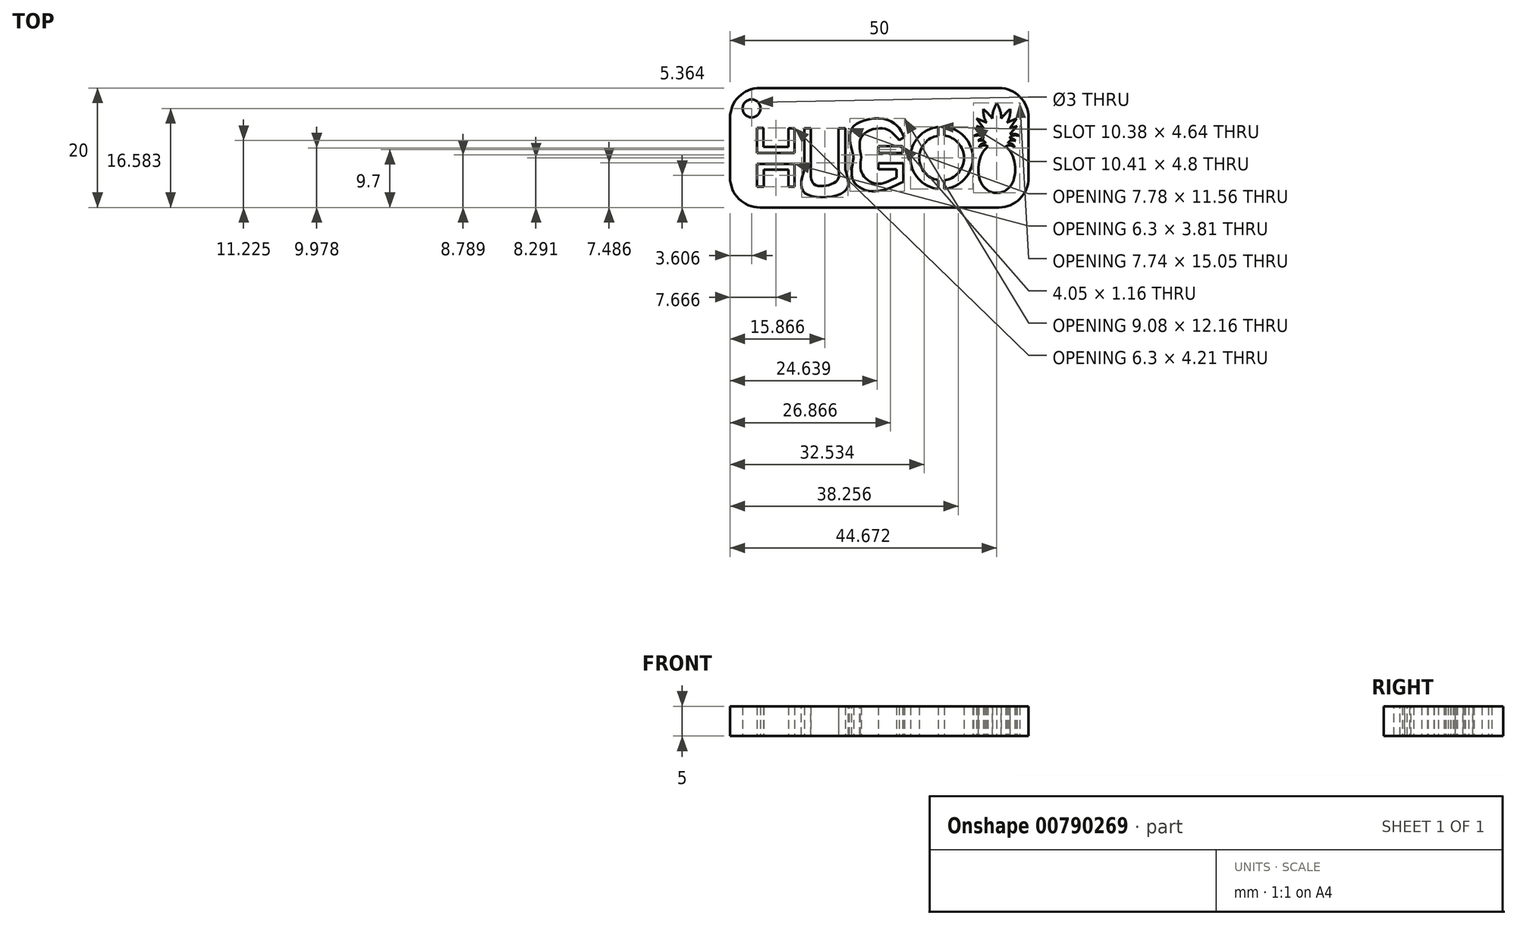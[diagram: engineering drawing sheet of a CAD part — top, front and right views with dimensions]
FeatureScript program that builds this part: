
annotation { "Feature Type Name" : "Feature", "Feature Type Description" : "" }
export const myFeature = defineFeature(function(context is Context, id is Id, definition is map)
    precondition{}
    {
        {
            var Q0;
            Q0=qCreatedBy(makeId("Top.planeOp"),FACE);
            var sketch = newSketch(context, id + "F0", { "sketchPlane" : qUnion([Q0])});
            skLineSegment(sketch, "E0.bottom", {"start": v(-19.84, 5.89) * mm, "end": v(20.16, 5.89) * mm});
            skLineSegment(sketch, "E0.top", {"start": v(-19.84, -14.11) * mm, "end": v(20.16, -14.11) * mm});
            skLineSegment(sketch, "E0.left", {"start": v(-24.84, 0.89) * mm, "end": v(-24.84, -9.11) * mm});
            skLineSegment(sketch, "E0.right", {"start": v(25.16, 0.89) * mm, "end": v(25.16, -9.11) * mm});
            skPoint(sketch, "E1.visualSharp", {"position": v(-24.84, 5.89) * mm});
            skArc(sketch, "E1.filletArc", {"start": v(-19.84, 5.89) * mm, "mid": v(-23.37, 4.42) * mm, "end": v(-24.84, 0.89) * mm});
            skPoint(sketch, "E2.visualSharp", {"position": v(-24.84, -14.11) * mm});
            skArc(sketch, "E2.filletArc", {"start": v(-24.84, -9.11) * mm, "mid": v(-23.37, -12.65) * mm, "end": v(-19.84, -14.11) * mm});
            skPoint(sketch, "E3.visualSharp", {"position": v(25.16, -14.11) * mm});
            skArc(sketch, "E3.filletArc", {"start": v(20.16, -14.11) * mm, "mid": v(23.7, -12.65) * mm, "end": v(25.16, -9.11) * mm});
            skPoint(sketch, "E4.visualSharp", {"position": v(25.16, 5.89) * mm});
            skArc(sketch, "E4.filletArc", {"start": v(25.16, 0.89) * mm, "mid": v(23.7, 4.42) * mm, "end": v(20.16, 5.89) * mm});
            skLineSegment(sketch, "E5", {"start": v(-18.48, 0.56) * mm, "end": v(-18.48, -3.26) * mm});
            skLineSegment(sketch, "E6", {"start": v(-18.48, -3.26) * mm, "end": v(-12.75, -3.26) * mm});
            skLineSegment(sketch, "E7", {"start": v(-12.75, -3.26) * mm, "end": v(-12.75, 0.5) * mm});
            skLineSegment(sketch, "E8", {"start": v(-12.75, 0.5) * mm, "end": v(-13.71, 0.5) * mm});
            skLineSegment(sketch, "E9", {"start": v(-13.71, 0.5) * mm, "end": v(-13.71, -2.33) * mm});
            skLineSegment(sketch, "E10", {"start": v(-13.71, -2.33) * mm, "end": v(-17.48, -2.33) * mm});
            skLineSegment(sketch, "E11", {"start": v(-17.48, -2.33) * mm, "end": v(-17.48, 0.56) * mm});
            skLineSegment(sketch, "E12", {"start": v(-17.48, 0.56) * mm, "end": v(-18.48, 0.56) * mm});
            skLineSegment(sketch, "E13", {"start": v(-18.48, -4.94) * mm, "end": v(-12.75, -4.94) * mm});
            skLineSegment(sketch, "E14", {"start": v(-12.75, -4.94) * mm, "end": v(-12.75, -8.41) * mm});
            skLineSegment(sketch, "E15", {"start": v(-12.75, -8.41) * mm, "end": v(-13.7, -8.41) * mm});
            skLineSegment(sketch, "E16", {"start": v(-13.7, -8.41) * mm, "end": v(-13.7, -5.81) * mm});
            skLineSegment(sketch, "E17", {"start": v(-13.7, -5.81) * mm, "end": v(-17.44, -5.81) * mm});
            skLineSegment(sketch, "E18", {"start": v(-17.44, -5.81) * mm, "end": v(-17.44, -8.41) * mm});
            skLineSegment(sketch, "E19", {"start": v(-10.28, 0.5) * mm, "end": v(-10.28, -5.77) * mm});
            skLineSegment(sketch, "E20", {"start": v(-10.28, 0.5) * mm, "end": v(-11.25, 0.5) * mm});
            skLineSegment(sketch, "E21", {"start": v(-11.25, 0.5) * mm, "end": v(-11.25, -5.77) * mm});
            skFitSpline(sketch, "E22", {"points": [v(-11.25, -5.77) * mm, v(-5.06, -5.77) * mm], "startDerivative": vector(0.22, -10.8) * mm, "endDerivative": vector(0.13, 9.96) * mm});
            skLineSegment(sketch, "E23", {"start": v(-5.06, -5.77) * mm, "end": v(-5.06, 0.5) * mm});
            skLineSegment(sketch, "E24", {"start": v(-5.06, 0.5) * mm, "end": v(-6.09, 0.5) * mm});
            skLineSegment(sketch, "E25", {"start": v(-6.09, 0.5) * mm, "end": v(-6.09, -5.77) * mm});
            skFitSpline(sketch, "E26", {"points": [v(-10.28, -5.77) * mm, v(-6.09, -5.77) * mm], "startDerivative": vector(1.86, -6.96) * mm, "endDerivative": vector(0.87, 5.34) * mm});
            skLineSegment(sketch, "E27", {"start": v(0, -2.21) * mm, "end": v(0, -3.26) * mm});
            skLineSegment(sketch, "E28", {"start": v(0, -3.26) * mm, "end": v(3.68, -3.26) * mm});
            skLineSegment(sketch, "E29", {"start": v(3.68, -3.26) * mm, "end": v(3.68, -2.21) * mm});
            skLineSegment(sketch, "E30", {"start": v(3.68, -2.21) * mm, "end": v(0, -2.21) * mm});
            skLineSegment(sketch, "E31", {"start": v(0, -4.83) * mm, "end": v(3.79, -4.83) * mm});
            skLineSegment(sketch, "E32", {"start": v(3.79, -4.83) * mm, "end": v(3.79, -7.64) * mm});
            skLineSegment(sketch, "E33", {"start": v(0, -4.83) * mm, "end": v(0, -5.76) * mm});
            skLineSegment(sketch, "E34", {"start": v(0, -5.76) * mm, "end": v(2.74, -5.76) * mm});
            skLineSegment(sketch, "E35", {"start": v(2.74, -5.76) * mm, "end": v(2.74, -6.98) * mm});
            skLineSegment(sketch, "E36", {"start": v(3.16, -1.32) * mm, "end": v(3.95, -0.82) * mm});
            skCircle(sketch, "E37", {"center": v(9.63, -4.02) * mm, "radius": 4.75 * mm});
            skCircle(sketch, "E38", {"center": v(9.63, -4.02) * mm, "radius": 3.42 * mm});
            skFitSpline(sketch, "E39", {"points": [v(18.36, -3.9) * mm, v(19.83, -11.66) * mm], "startDerivative": vector(-7.27, -5.5) * mm, "endDerivative": vector(11.16, -0.02) * mm});
            skFitSpline(sketch, "E40", {"points": [v(18.36, -3.9) * mm, v(16.84, -4.02) * mm], "startDerivative": vector(-0.8, 0.54) * mm, "endDerivative": vector(-2.6, -1.65) * mm});
            skFitSpline(sketch, "E41", {"points": [v(16.84, -4.02) * mm, v(17.98, -3.35) * mm], "startDerivative": vector(0.44, 1.12) * mm, "endDerivative": vector(2.28, -0.1) * mm});
            skFitSpline(sketch, "E42", {"points": [v(17.98, -3.35) * mm, v(16.69, -2.95) * mm], "startDerivative": vector(-0.63, 1.38) * mm, "endDerivative": vector(-2.13, -0.57) * mm});
            skFitSpline(sketch, "E43", {"points": [v(16.69, -2.95) * mm, v(17.7, -2.5) * mm], "startDerivative": vector(0.87, 1.1) * mm, "endDerivative": vector(1.28, 0.15) * mm});
            skFitSpline(sketch, "E44", {"points": [v(17.7, -2.5) * mm, v(15.96, -2.15) * mm], "startDerivative": vector(-1.13, 1.33) * mm, "endDerivative": vector(-2.84, -0.77) * mm});
            skFitSpline(sketch, "E45", {"points": [v(15.96, -2.15) * mm, v(17.66, -1.83) * mm], "startDerivative": vector(1.53, 0.99) * mm, "endDerivative": vector(2.26, -0.37) * mm});
            skLineSegment(sketch, "E46", {"start": v(17.66, -1.83) * mm, "end": v(16.45, -0.46) * mm});
            skLineSegment(sketch, "E47", {"start": v(16.45, -0.46) * mm, "end": v(17.66, -0.87) * mm});
            skLineSegment(sketch, "E48", {"start": v(17.66, -0.87) * mm, "end": v(16.47, 0.8) * mm});
            skLineSegment(sketch, "E49", {"start": v(16.47, 0.8) * mm, "end": v(18.15, 0.08) * mm});
            skFitSpline(sketch, "E50", {"points": [v(18.15, 0.08) * mm, v(17.55, 2.36) * mm], "startDerivative": vector(-1.53, 2.07) * mm, "endDerivative": vector(-0.1, 2.34) * mm});
            skFitSpline(sketch, "E51", {"points": [v(17.55, 2.36) * mm, v(19.09, 0.8) * mm], "startDerivative": vector(1.69, -1.38) * mm, "endDerivative": vector(1.38, -1.77) * mm});
            skFitSpline(sketch, "E52", {"points": [v(19.09, 0.8) * mm, v(19.83, 3.4) * mm], "startDerivative": vector(-0.13, 3.12) * mm, "endDerivative": vector(1.04, 1.95) * mm});
            skLineSegment(sketch, "E53", {"start": v(19.83, 3.4) * mm, "end": v(19.83, -11.62) * mm});
            skFitSpline(sketch, "E54.MirrorCS", {"points": [v(21.95, -2.5) * mm, v(23.7, -2.15) * mm], "startDerivative": vector(1.13, 1.33) * mm, "endDerivative": vector(2.84, -0.77) * mm});
            skFitSpline(sketch, "E55.MirrorCS", {"points": [v(23.7, -2.15) * mm, v(22, -1.83) * mm], "startDerivative": vector(-1.53, 0.99) * mm, "endDerivative": vector(-2.26, -0.37) * mm});
            skFitSpline(sketch, "E56.MirrorCS", {"points": [v(20.58, 0.8) * mm, v(19.83, 3.4) * mm], "startDerivative": vector(0.13, 3.12) * mm, "endDerivative": vector(-1.04, 1.95) * mm});
            skFitSpline(sketch, "E57.MirrorCS", {"points": [v(22.97, -2.95) * mm, v(21.95, -2.5) * mm], "startDerivative": vector(-0.87, 1.1) * mm, "endDerivative": vector(-1.28, 0.15) * mm});
            skFitSpline(sketch, "E58.MirrorCS", {"points": [v(21.3, -3.9) * mm, v(22.83, -4.02) * mm], "startDerivative": vector(0.8, 0.54) * mm, "endDerivative": vector(2.6, -1.65) * mm});
            skFitSpline(sketch, "E59.MirrorCS", {"points": [v(22.11, 2.36) * mm, v(20.58, 0.8) * mm], "startDerivative": vector(-1.69, -1.38) * mm, "endDerivative": vector(-1.38, -1.77) * mm});
            skFitSpline(sketch, "E60.MirrorCS", {"points": [v(22.83, -4.02) * mm, v(21.68, -3.35) * mm], "startDerivative": vector(-0.44, 1.12) * mm, "endDerivative": vector(-2.28, -0.1) * mm});
            skLineSegment(sketch, "E61.MirrorCS", {"start": v(22, -1.83) * mm, "end": v(23.22, -0.46) * mm});
            skFitSpline(sketch, "E62.MirrorCS", {"points": [v(21.51, 0.08) * mm, v(22.11, 2.36) * mm], "startDerivative": vector(1.53, 2.07) * mm, "endDerivative": vector(0.1, 2.34) * mm});
            skFitSpline(sketch, "E63.MirrorCS", {"points": [v(21.68, -3.35) * mm, v(22.97, -2.95) * mm], "startDerivative": vector(0.63, 1.38) * mm, "endDerivative": vector(2.13, -0.57) * mm});
            skLineSegment(sketch, "E64.MirrorCS", {"start": v(23.2, 0.8) * mm, "end": v(21.51, 0.08) * mm});
            skLineSegment(sketch, "E65.MirrorCS", {"start": v(59.5, 5.89) * mm, "end": v(19.5, 5.89) * mm});
            skLineSegment(sketch, "E66.MirrorCS", {"start": v(22, -0.87) * mm, "end": v(23.2, 0.8) * mm});
            skFitSpline(sketch, "E67.MirrorCS", {"points": [v(21.3, -3.9) * mm, v(19.83, -11.66) * mm], "startDerivative": vector(7.27, -5.5) * mm, "endDerivative": vector(-11.16, -0.02) * mm});
            skLineSegment(sketch, "E68.MirrorCS", {"start": v(23.22, -0.46) * mm, "end": v(22, -0.87) * mm});
            skLineSegment(sketch, "E69", {"start": v(-17.44, -8.41) * mm, "end": v(-18.48, -8.41) * mm});
            skLineSegment(sketch, "E70", {"start": v(-18.48, -8.41) * mm, "end": v(-18.48, -4.94) * mm});
            skFitSpline(sketch, "E71", {"points": [v(3.79, -7.64) * mm, v(-3.76, -3.9) * mm], "startDerivative": vector(-13.3, -4.36) * mm, "endDerivative": vector(-0.15, 11.36) * mm});
            skFitSpline(sketch, "E72", {"points": [v(-3.76, -3.9) * mm, v(3.95, -0.82) * mm], "startDerivative": vector(-0.24, 13.91) * mm, "endDerivative": vector(7.19, -7.64) * mm});
            skFitSpline(sketch, "E73", {"points": [v(-2.6, -3.96) * mm, v(2.74, -6.98) * mm], "startDerivative": vector(0.11, -6.75) * mm, "endDerivative": vector(9.48, 2.83) * mm});
            skFitSpline(sketch, "E74", {"points": [v(-2.6, -3.96) * mm, v(3.16, -1.32) * mm], "startDerivative": vector(0.46, 10.07) * mm, "endDerivative": vector(6.53, -5.23) * mm});
            skLineSegment(sketch, "E75", {"start": v(19.83, -11.62) * mm, "end": v(19.83, -14.11) * mm});
            skLineSegment(sketch, "E76", {"start": v(19.83, 3.4) * mm, "end": v(19.83, 5.89) * mm});
            skLineSegment(sketch, "E77", {"start": v(9.38, -7.43) * mm, "end": v(9.38, -8.76) * mm});
            skLineSegment(sketch, "E78", {"start": v(9.88, -7.43) * mm, "end": v(9.88, -8.76) * mm});
            skLineSegment(sketch, "E79", {"start": v(9.63, -4.02) * mm, "end": v(13.05, -4.02) * mm});
            skLineSegment(sketch, "E80.MirrorCS", {"start": v(9.88, -0.6) * mm, "end": v(9.88, 0.72) * mm});
            skLineSegment(sketch, "E81.MirrorCS", {"start": v(9.38, -0.6) * mm, "end": v(9.38, 0.72) * mm});
            skCircle(sketch, "E82", {"center": v(-21.23, 2.47) * mm, "radius": 1.5 * mm});
            skSolve(sketch);
        }
        {
            var Q0;
            Q0 = qSketchRegion(id + "F0", true);
            var Q1;
            {var subQ0=sQuery(id+"F0.wireOp",EDGE,"E77");Q1=makeQuery(id+"F0.imprint","IMPRINT",FACE,{"disambiguationData":[TD([[makeQuery(id+"F0.imprint","IMPRINT",EDGE,{"derivedFrom":subQ0}),1.0]])]});}
            var Q2;
            {var subQ0=sQuery(id+"F0.wireOp",EDGE,"E38");var subQ5=makeQuery(id+"F0.imprint","IMPRINT",VERTEX,{"derivedFrom":subQ0});Q2=makeQuery(id+"F0.imprint","IMPRINT",FACE,{"disambiguationData":[TD([[makeQuery(id+"F0.imprint","IMPRINT",EDGE,{"disambiguationData":[TD([[subQ5,-1.0]])],"derivedFrom":subQ0}),1.0]])]});}
            var Q3;
            {var subQ0=sQuery(id+"F0.wireOp",EDGE,"E80.MirrorCS");Q3=makeQuery(id+"F0.imprint","IMPRINT",FACE,{"disambiguationData":[TD([[makeQuery(id+"F0.imprint","IMPRINT",EDGE,{"derivedFrom":subQ0}),1.0]])]});}
            var Q4;
            Q4=makeQuery(id+"F0.imprint","IMPRINT",FACE,{"disambiguationData":[TD([[makeQuery(id+"F0.imprint","IMPRINT",EDGE,{"derivedFrom":sQuery(id+"F0.wireOp",EDGE,"E5")}),1.0]])]});
            var Q5;
            Q5=makeQuery(id+"F0.imprint","IMPRINT",FACE,{"disambiguationData":[TD([[makeQuery(id+"F0.imprint","IMPRINT",EDGE,{"derivedFrom":sQuery(id+"F0.wireOp",EDGE,"E13")}),-1.0]])]});
            var Q6;
            Q6=makeQuery(id+"F0.imprint","IMPRINT",FACE,{"disambiguationData":[TD([[makeQuery(id+"F0.imprint","IMPRINT",EDGE,{"derivedFrom":sQuery(id+"F0.wireOp",EDGE,"E19")}),-1.0]])]});
            var Q7;
            Q7=makeQuery(id+"F0.imprint","IMPRINT",FACE,{"disambiguationData":[TD([[makeQuery(id+"F0.imprint","IMPRINT",EDGE,{"derivedFrom":sQuery(id+"F0.wireOp",EDGE,"E31")}),-1.0]])]});
            var Q8;
            Q8=makeQuery(id+"F0.imprint","IMPRINT",FACE,{"disambiguationData":[TD([[makeQuery(id+"F0.imprint","IMPRINT",EDGE,{"derivedFrom":sQuery(id+"F0.wireOp",EDGE,"E27")}),1.0]])]});
            var Q9;
            {var subQ0=sQuery(id+"F0.wireOp",EDGE,"E77");Q9=makeQuery(id+"F0.imprint","IMPRINT",FACE,{"disambiguationData":[TD([[makeQuery(id+"F0.imprint","IMPRINT",EDGE,{"derivedFrom":subQ0}),-1.0]])]});}
            var Q10;
            {var subQ0=sQuery(id+"F0.wireOp",EDGE,"E78");Q10=makeQuery(id+"F0.imprint","IMPRINT",FACE,{"disambiguationData":[TD([[makeQuery(id+"F0.imprint","IMPRINT",EDGE,{"derivedFrom":subQ0}),1.0]])]});}
            extrude(context, id + "F1", {"entities" : qUnion([Q0, Q1, Q2, Q3, Q4, Q5, Q6, Q7, Q8, Q9, Q10]), "depth" : 5 * mm, "offsetDistance" : 25 * mm});
        }
        {
            var Q0;
            Q0=makeQuery(id+"F1.opExtrude","CAP_FACE",FACE,{"disambiguationData":[OSD([sQuery(id+"F0.wireOp",EDGE,"E0.bottom"),sQuery(id+"F0.wireOp",EDGE,"E0.top"),sQuery(id+"F0.wireOp",EDGE,"E0.left"),sQuery(id+"F0.wireOp",EDGE,"E0.right"),sQuery(id+"F0.wireOp",EDGE,"E1.filletArc"),sQuery(id+"F0.wireOp",EDGE,"E2.filletArc"),sQuery(id+"F0.wireOp",EDGE,"E3.filletArc"),sQuery(id+"F0.wireOp",EDGE,"E4.filletArc"),sQuery(id+"F0.wireOp",EDGE,"E5"),sQuery(id+"F0.wireOp",EDGE,"E6"),sQuery(id+"F0.wireOp",EDGE,"E7"),sQuery(id+"F0.wireOp",EDGE,"E8"),sQuery(id+"F0.wireOp",EDGE,"E9"),sQuery(id+"F0.wireOp",EDGE,"E10"),sQuery(id+"F0.wireOp",EDGE,"E11"),sQuery(id+"F0.wireOp",EDGE,"E12"),sQuery(id+"F0.wireOp",EDGE,"E13"),sQuery(id+"F0.wireOp",EDGE,"E14"),sQuery(id+"F0.wireOp",EDGE,"E15"),sQuery(id+"F0.wireOp",EDGE,"E16"),sQuery(id+"F0.wireOp",EDGE,"E17"),sQuery(id+"F0.wireOp",EDGE,"E18"),sQuery(id+"F0.wireOp",EDGE,"E19"),sQuery(id+"F0.wireOp",EDGE,"E20"),sQuery(id+"F0.wireOp",EDGE,"E21"),sQuery(id+"F0.wireOp",EDGE,"E22"),sQuery(id+"F0.wireOp",EDGE,"E23"),sQuery(id+"F0.wireOp",EDGE,"E24"),sQuery(id+"F0.wireOp",EDGE,"E25"),sQuery(id+"F0.wireOp",EDGE,"E26"),sQuery(id+"F0.wireOp",EDGE,"E27"),sQuery(id+"F0.wireOp",EDGE,"E28"),sQuery(id+"F0.wireOp",EDGE,"E29"),sQuery(id+"F0.wireOp",EDGE,"E30"),sQuery(id+"F0.wireOp",EDGE,"E31"),sQuery(id+"F0.wireOp",EDGE,"E32"),sQuery(id+"F0.wireOp",EDGE,"E33"),sQuery(id+"F0.wireOp",EDGE,"E34"),sQuery(id+"F0.wireOp",EDGE,"E35"),sQuery(id+"F0.wireOp",EDGE,"E36"),sQuery(id+"F0.wireOp",EDGE,"E37"),sQuery(id+"F0.wireOp",EDGE,"E38"),sQuery(id+"F0.wireOp",EDGE,"E39"),sQuery(id+"F0.wireOp",EDGE,"E40"),sQuery(id+"F0.wireOp",EDGE,"E41"),sQuery(id+"F0.wireOp",EDGE,"E42"),sQuery(id+"F0.wireOp",EDGE,"E43"),sQuery(id+"F0.wireOp",EDGE,"E44"),sQuery(id+"F0.wireOp",EDGE,"E45"),sQuery(id+"F0.wireOp",EDGE,"E46"),sQuery(id+"F0.wireOp",EDGE,"E47"),sQuery(id+"F0.wireOp",EDGE,"E48"),sQuery(id+"F0.wireOp",EDGE,"E49"),sQuery(id+"F0.wireOp",EDGE,"E50"),sQuery(id+"F0.wireOp",EDGE,"E51"),sQuery(id+"F0.wireOp",EDGE,"E52"),sQuery(id+"F0.wireOp",EDGE,"E54.MirrorCS"),sQuery(id+"F0.wireOp",EDGE,"E55.MirrorCS"),sQuery(id+"F0.wireOp",EDGE,"E56.MirrorCS"),sQuery(id+"F0.wireOp",EDGE,"E57.MirrorCS"),sQuery(id+"F0.wireOp",EDGE,"E58.MirrorCS"),sQuery(id+"F0.wireOp",EDGE,"E59.MirrorCS"),sQuery(id+"F0.wireOp",EDGE,"E60.MirrorCS"),sQuery(id+"F0.wireOp",EDGE,"E61.MirrorCS"),sQuery(id+"F0.wireOp",EDGE,"E62.MirrorCS"),sQuery(id+"F0.wireOp",EDGE,"E63.MirrorCS"),sQuery(id+"F0.wireOp",EDGE,"E64.MirrorCS"),sQuery(id+"F0.wireOp",EDGE,"E65.MirrorCS"),sQuery(id+"F0.wireOp",EDGE,"E66.MirrorCS"),sQuery(id+"F0.wireOp",EDGE,"E67.MirrorCS"),sQuery(id+"F0.wireOp",EDGE,"E68.MirrorCS"),sQuery(id+"F0.wireOp",EDGE,"E69"),sQuery(id+"F0.wireOp",EDGE,"E70"),sQuery(id+"F0.wireOp",EDGE,"E71"),sQuery(id+"F0.wireOp",EDGE,"E72"),sQuery(id+"F0.wireOp",EDGE,"E73"),sQuery(id+"F0.wireOp",EDGE,"E74"),sQuery(id+"F0.wireOp",EDGE,"E77"),sQuery(id+"F0.wireOp",EDGE,"E78"),sQuery(id+"F0.wireOp",EDGE,"E80.MirrorCS"),sQuery(id+"F0.wireOp",EDGE,"E81.MirrorCS"),sQuery(id+"F0.wireOp",EDGE,"E82")])],"isStart":false});
            var sketch = newSketch(context, id + "F2", { "sketchPlane" : qUnion([Q0])});
            skLineSegment(sketch, "E83.0", {"start": v(-13.7, -8.41) * mm, "end": v(-13.7, -5.81) * mm});
            skLineSegment(sketch, "E83.1", {"start": v(3.79, -4.83) * mm, "end": v(3.79, -7.64) * mm});
            skLineSegment(sketch, "E83.2", {"start": v(-13.7, -5.81) * mm, "end": v(-17.44, -5.81) * mm});
            skLineSegment(sketch, "E83.3", {"start": v(-17.44, -5.81) * mm, "end": v(-17.44, -8.41) * mm});
            skLineSegment(sketch, "E83.4", {"start": v(0, -5.76) * mm, "end": v(2.74, -5.76) * mm});
            skLineSegment(sketch, "E83.5", {"start": v(-10.28, 0.5) * mm, "end": v(-10.28, -5.77) * mm});
            skCircle(sketch, "E83.6", {"center": v(9.63, -4.02) * mm, "radius": 4.75 * mm});
            skLineSegment(sketch, "E83.7", {"start": v(-11.25, 0.5) * mm, "end": v(-11.25, -5.77) * mm});
            skCircle(sketch, "E83.8", {"center": v(9.63, -4.02) * mm, "radius": 3.42 * mm});
            skFitSpline(sketch, "E83.9", {"points": [v(-11.25, -5.77) * mm, v(-11.17, -9.38) * mm, v(-5.1, -9.1) * mm, v(-5.06, -5.77) * mm]});
            skLineSegment(sketch, "E83.10", {"start": v(-18.48, -8.41) * mm, "end": v(-18.48, -4.94) * mm});
            skLineSegment(sketch, "E83.11", {"start": v(-5.06, -5.77) * mm, "end": v(-5.06, 0.5) * mm});
            skFitSpline(sketch, "E83.12", {"points": [v(3.79, -7.64) * mm, v(-0.64, -9.1) * mm, v(-3.71, -7.68) * mm, v(-3.76, -3.9) * mm]});
            skFitSpline(sketch, "E83.13", {"points": [v(-3.76, -3.9) * mm, v(-3.84, 0.74) * mm, v(1.55, 1.73) * mm, v(3.95, -0.82) * mm]});
            skFitSpline(sketch, "E83.14", {"points": [v(-2.6, -3.96) * mm, v(-2.45, -0.6) * mm, v(0.99, 0.42) * mm, v(3.16, -1.32) * mm]});
            skFitSpline(sketch, "E83.15", {"points": [v(-10.28, -5.77) * mm, v(-9.66, -8.1) * mm, v(-6.38, -7.55) * mm, v(-6.09, -5.77) * mm]});
            skLineSegment(sketch, "E83.16", {"start": v(-6.09, 0.5) * mm, "end": v(-6.09, -5.77) * mm});
            skFitSpline(sketch, "E83.17", {"points": [v(-2.6, -3.96) * mm, v(-2.56, -6.21) * mm, v(-0.42, -7.93) * mm, v(2.74, -6.98) * mm]});
            skLineSegment(sketch, "E83.18", {"start": v(0, -3.26) * mm, "end": v(3.68, -3.26) * mm});
            skLineSegment(sketch, "E83.19", {"start": v(-13.71, -2.33) * mm, "end": v(-17.48, -2.33) * mm});
            skLineSegment(sketch, "E83.20", {"start": v(-17.48, -2.33) * mm, "end": v(-17.48, 0.56) * mm});
            skLineSegment(sketch, "E83.21", {"start": v(-18.48, 0.56) * mm, "end": v(-18.48, -3.26) * mm});
            skLineSegment(sketch, "E83.22", {"start": v(-18.48, -3.26) * mm, "end": v(-12.75, -3.26) * mm});
            skLineSegment(sketch, "E83.23", {"start": v(-12.75, -3.26) * mm, "end": v(-12.75, 0.5) * mm});
            skLineSegment(sketch, "E83.24", {"start": v(-13.71, 0.5) * mm, "end": v(-13.71, -2.33) * mm});
            skLineSegment(sketch, "E83.25", {"start": v(-18.48, -4.94) * mm, "end": v(-12.75, -4.94) * mm});
            skLineSegment(sketch, "E83.26", {"start": v(-12.75, -4.94) * mm, "end": v(-12.75, -8.41) * mm});
            skLineSegment(sketch, "E83.27", {"start": v(3.68, -2.21) * mm, "end": v(0, -2.21) * mm});
            skLineSegment(sketch, "E83.28", {"start": v(9.63, -4.02) * mm, "end": v(13.05, -4.02) * mm, "construction": true});
            skLineSegment(sketch, "E83.29", {"start": v(0, -4.83) * mm, "end": v(3.79, -4.83) * mm});
            skLineSegment(sketch, "E84", {"start": v(2.74, -5.76) * mm, "end": v(2.74, -6.98) * mm});
            skLineSegment(sketch, "E85", {"start": v(0, -4.83) * mm, "end": v(0, -5.76) * mm});
            skLineSegment(sketch, "E86", {"start": v(0, -2.21) * mm, "end": v(0, -3.26) * mm});
            skLineSegment(sketch, "E87", {"start": v(3.68, -2.21) * mm, "end": v(3.68, -3.26) * mm});
            skLineSegment(sketch, "E88", {"start": v(3.16, -1.32) * mm, "end": v(3.95, -0.82) * mm});
            skLineSegment(sketch, "E89", {"start": v(-11.25, 0.5) * mm, "end": v(-10.28, 0.5) * mm});
            skLineSegment(sketch, "E90", {"start": v(-6.09, 0.5) * mm, "end": v(-5.06, 0.5) * mm});
            skLineSegment(sketch, "E91", {"start": v(-13.71, 0.5) * mm, "end": v(-12.75, 0.5) * mm});
            skLineSegment(sketch, "E92", {"start": v(-17.48, 0.56) * mm, "end": v(-18.48, 0.56) * mm});
            skLineSegment(sketch, "E93", {"start": v(-18.48, -8.41) * mm, "end": v(-17.44, -8.41) * mm});
            skLineSegment(sketch, "E94", {"start": v(-13.7, -8.41) * mm, "end": v(-12.75, -8.41) * mm});
            skLineSegment(sketch, "E95.0", {"start": v(9.38, -7.43) * mm, "end": v(9.38, -8.76) * mm});
            skLineSegment(sketch, "E96.0", {"start": v(9.88, -7.43) * mm, "end": v(9.88, -8.76) * mm});
            skLineSegment(sketch, "E97.0", {"start": v(9.38, -0.6) * mm, "end": v(9.38, 0.72) * mm});
            skLineSegment(sketch, "E98.0", {"start": v(9.88, -0.6) * mm, "end": v(9.88, 0.72) * mm});
            skSolve(sketch);
        }
        {
            var Q0;
            Q0 = qSketchRegion(id + "F2", true);
            extrude(context, id + "F3", {"entities" : qUnion([Q0]), "depth" : 25 * mm, "offsetDistance" : 25 * mm});
        }
        {
            var Q0;
            Q0=makeQuery(id+"F3.opExtrude","SWEPT_BODY",BODY,{"disambiguationData":[OSD([sQuery(id+"F2.wireOp",EDGE,"E83.0"),sQuery(id+"F2.wireOp",EDGE,"E83.2"),sQuery(id+"F2.wireOp",EDGE,"E83.3"),sQuery(id+"F2.wireOp",EDGE,"E83.10"),sQuery(id+"F2.wireOp",EDGE,"E83.25"),sQuery(id+"F2.wireOp",EDGE,"E83.26"),sQuery(id+"F2.wireOp",EDGE,"E93"),sQuery(id+"F2.wireOp",EDGE,"E94")])]});
            var Q1;
            Q1=makeQuery(id+"F3.opExtrude","SWEPT_BODY",BODY,{"disambiguationData":[OSD([sQuery(id+"F2.wireOp",EDGE,"E83.1"),sQuery(id+"F2.wireOp",EDGE,"E83.4"),sQuery(id+"F2.wireOp",EDGE,"E83.12"),sQuery(id+"F2.wireOp",EDGE,"E83.13"),sQuery(id+"F2.wireOp",EDGE,"E83.14"),sQuery(id+"F2.wireOp",EDGE,"E83.17"),sQuery(id+"F2.wireOp",EDGE,"E83.29"),sQuery(id+"F2.wireOp",EDGE,"E84"),sQuery(id+"F2.wireOp",EDGE,"E85"),sQuery(id+"F2.wireOp",EDGE,"E88")])]});
            var Q2;
            Q2=makeQuery(id+"F3.opExtrude","SWEPT_BODY",BODY,{"disambiguationData":[OSD([sQuery(id+"F2.wireOp",EDGE,"E83.5"),sQuery(id+"F2.wireOp",EDGE,"E83.7"),sQuery(id+"F2.wireOp",EDGE,"E83.9"),sQuery(id+"F2.wireOp",EDGE,"E83.11"),sQuery(id+"F2.wireOp",EDGE,"E83.15"),sQuery(id+"F2.wireOp",EDGE,"E83.16"),sQuery(id+"F2.wireOp",EDGE,"E89"),sQuery(id+"F2.wireOp",EDGE,"E90")])]});
            var Q3;
            Q3=makeQuery(id+"F3.opExtrude","SWEPT_BODY",BODY,{"disambiguationData":[OSD([sQuery(id+"F2.wireOp",EDGE,"E83.6"),sQuery(id+"F2.wireOp",EDGE,"E83.8")])]});
            var Q4;
            Q4=makeQuery(id+"F3.opExtrude","SWEPT_BODY",BODY,{"disambiguationData":[OSD([sQuery(id+"F2.wireOp",EDGE,"E83.18"),sQuery(id+"F2.wireOp",EDGE,"E83.27"),sQuery(id+"F2.wireOp",EDGE,"E86"),sQuery(id+"F2.wireOp",EDGE,"E87")])]});
            var Q5;
            Q5=makeQuery(id+"F3.opExtrude","SWEPT_BODY",BODY,{"disambiguationData":[OSD([sQuery(id+"F2.wireOp",EDGE,"E83.19"),sQuery(id+"F2.wireOp",EDGE,"E83.20"),sQuery(id+"F2.wireOp",EDGE,"E83.21"),sQuery(id+"F2.wireOp",EDGE,"E83.22"),sQuery(id+"F2.wireOp",EDGE,"E83.23"),sQuery(id+"F2.wireOp",EDGE,"E83.24"),sQuery(id+"F2.wireOp",EDGE,"E91"),sQuery(id+"F2.wireOp",EDGE,"E92")])]});
            var Q6;
            Q6=qCreatedBy(makeId("Origin.pointOp"),VERTEX);
            transform(context, id + "F4", {"entities" : qUnion([Q0, Q1, Q2, Q3, Q4, Q5]), "transformType" : TransformType.SCALE_UNIFORMLY, "scale" : 1.1, "scalePoint" : qUnion([Q6]), "makeCopy" : false});
        }
        {
            var Q0;
            Q0=makeQuery(id+"F3.opExtrude","SWEPT_BODY",BODY,{"disambiguationData":[OSD([sQuery(id+"F2.wireOp",EDGE,"E83.0"),sQuery(id+"F2.wireOp",EDGE,"E83.2"),sQuery(id+"F2.wireOp",EDGE,"E83.3"),sQuery(id+"F2.wireOp",EDGE,"E83.10"),sQuery(id+"F2.wireOp",EDGE,"E83.25"),sQuery(id+"F2.wireOp",EDGE,"E83.26"),sQuery(id+"F2.wireOp",EDGE,"E93"),sQuery(id+"F2.wireOp",EDGE,"E94")])]});
            var Q1;
            Q1=makeQuery(id+"F3.opExtrude","SWEPT_BODY",BODY,{"disambiguationData":[OSD([sQuery(id+"F2.wireOp",EDGE,"E83.1"),sQuery(id+"F2.wireOp",EDGE,"E83.4"),sQuery(id+"F2.wireOp",EDGE,"E83.12"),sQuery(id+"F2.wireOp",EDGE,"E83.13"),sQuery(id+"F2.wireOp",EDGE,"E83.14"),sQuery(id+"F2.wireOp",EDGE,"E83.17"),sQuery(id+"F2.wireOp",EDGE,"E83.29"),sQuery(id+"F2.wireOp",EDGE,"E84"),sQuery(id+"F2.wireOp",EDGE,"E85"),sQuery(id+"F2.wireOp",EDGE,"E88")])]});
            var Q2;
            Q2=makeQuery(id+"F3.opExtrude","SWEPT_BODY",BODY,{"disambiguationData":[OSD([sQuery(id+"F2.wireOp",EDGE,"E83.5"),sQuery(id+"F2.wireOp",EDGE,"E83.7"),sQuery(id+"F2.wireOp",EDGE,"E83.9"),sQuery(id+"F2.wireOp",EDGE,"E83.11"),sQuery(id+"F2.wireOp",EDGE,"E83.15"),sQuery(id+"F2.wireOp",EDGE,"E83.16"),sQuery(id+"F2.wireOp",EDGE,"E89"),sQuery(id+"F2.wireOp",EDGE,"E90")])]});
            var Q3;
            Q3=makeQuery(id+"F3.opExtrude","SWEPT_BODY",BODY,{"disambiguationData":[OSD([sQuery(id+"F2.wireOp",EDGE,"E83.6"),sQuery(id+"F2.wireOp",EDGE,"E83.8")])]});
            var Q4;
            Q4=makeQuery(id+"F3.opExtrude","SWEPT_BODY",BODY,{"disambiguationData":[OSD([sQuery(id+"F2.wireOp",EDGE,"E83.18"),sQuery(id+"F2.wireOp",EDGE,"E83.27"),sQuery(id+"F2.wireOp",EDGE,"E86"),sQuery(id+"F2.wireOp",EDGE,"E87")])]});
            var Q5;
            Q5=makeQuery(id+"F3.opExtrude","SWEPT_BODY",BODY,{"disambiguationData":[OSD([sQuery(id+"F2.wireOp",EDGE,"E83.19"),sQuery(id+"F2.wireOp",EDGE,"E83.20"),sQuery(id+"F2.wireOp",EDGE,"E83.21"),sQuery(id+"F2.wireOp",EDGE,"E83.22"),sQuery(id+"F2.wireOp",EDGE,"E83.23"),sQuery(id+"F2.wireOp",EDGE,"E83.24"),sQuery(id+"F2.wireOp",EDGE,"E91"),sQuery(id+"F2.wireOp",EDGE,"E92")])]});
            transform(context, id + "F5", {"entities" : qUnion([Q0, Q1, Q2, Q3, Q4, Q5]), "transformType" : TransformType.TRANSLATION_3D, "dx" : 0 * mm, "dy" : -1.4 * mm, "dz" : -11 * mm, "makeCopy" : false});
        }
        {
            var Q0;
            Q0=makeQuery(id+"F3.opExtrude","SWEPT_BODY",BODY,{"disambiguationData":[OSD([sQuery(id+"F2.wireOp",EDGE,"E83.0"),sQuery(id+"F2.wireOp",EDGE,"E83.2"),sQuery(id+"F2.wireOp",EDGE,"E83.3"),sQuery(id+"F2.wireOp",EDGE,"E83.10"),sQuery(id+"F2.wireOp",EDGE,"E83.25"),sQuery(id+"F2.wireOp",EDGE,"E83.26"),sQuery(id+"F2.wireOp",EDGE,"E93"),sQuery(id+"F2.wireOp",EDGE,"E94")])]});
            var Q1;
            Q1=makeQuery(id+"F3.opExtrude","SWEPT_BODY",BODY,{"disambiguationData":[OSD([sQuery(id+"F2.wireOp",EDGE,"E83.1"),sQuery(id+"F2.wireOp",EDGE,"E83.4"),sQuery(id+"F2.wireOp",EDGE,"E83.12"),sQuery(id+"F2.wireOp",EDGE,"E83.13"),sQuery(id+"F2.wireOp",EDGE,"E83.14"),sQuery(id+"F2.wireOp",EDGE,"E83.17"),sQuery(id+"F2.wireOp",EDGE,"E83.29"),sQuery(id+"F2.wireOp",EDGE,"E84"),sQuery(id+"F2.wireOp",EDGE,"E85"),sQuery(id+"F2.wireOp",EDGE,"E88")])]});
            var Q2;
            Q2=makeQuery(id+"F3.opExtrude","SWEPT_BODY",BODY,{"disambiguationData":[OSD([sQuery(id+"F2.wireOp",EDGE,"E83.5"),sQuery(id+"F2.wireOp",EDGE,"E83.7"),sQuery(id+"F2.wireOp",EDGE,"E83.9"),sQuery(id+"F2.wireOp",EDGE,"E83.11"),sQuery(id+"F2.wireOp",EDGE,"E83.15"),sQuery(id+"F2.wireOp",EDGE,"E83.16"),sQuery(id+"F2.wireOp",EDGE,"E89"),sQuery(id+"F2.wireOp",EDGE,"E90")])]});
            var Q3;
            Q3=makeQuery(id+"F3.opExtrude","SWEPT_BODY",BODY,{"disambiguationData":[OSD([sQuery(id+"F2.wireOp",EDGE,"E83.6"),sQuery(id+"F2.wireOp",EDGE,"E83.8")])]});
            var Q4;
            Q4=makeQuery(id+"F3.opExtrude","SWEPT_BODY",BODY,{"disambiguationData":[OSD([sQuery(id+"F2.wireOp",EDGE,"E83.18"),sQuery(id+"F2.wireOp",EDGE,"E83.27"),sQuery(id+"F2.wireOp",EDGE,"E86"),sQuery(id+"F2.wireOp",EDGE,"E87")])]});
            var Q5;
            Q5=makeQuery(id+"F3.opExtrude","SWEPT_BODY",BODY,{"disambiguationData":[OSD([sQuery(id+"F2.wireOp",EDGE,"E83.19"),sQuery(id+"F2.wireOp",EDGE,"E83.20"),sQuery(id+"F2.wireOp",EDGE,"E83.21"),sQuery(id+"F2.wireOp",EDGE,"E83.22"),sQuery(id+"F2.wireOp",EDGE,"E83.23"),sQuery(id+"F2.wireOp",EDGE,"E83.24"),sQuery(id+"F2.wireOp",EDGE,"E91"),sQuery(id+"F2.wireOp",EDGE,"E92")])]});
            var Q6;
            Q6=makeQuery(id+"F1.opExtrude","SWEPT_BODY",BODY,{"disambiguationData":[OSD([sQuery(id+"F0.wireOp",EDGE,"E0.bottom"),sQuery(id+"F0.wireOp",EDGE,"E0.top"),sQuery(id+"F0.wireOp",EDGE,"E0.left"),sQuery(id+"F0.wireOp",EDGE,"E0.right"),sQuery(id+"F0.wireOp",EDGE,"E1.filletArc"),sQuery(id+"F0.wireOp",EDGE,"E2.filletArc"),sQuery(id+"F0.wireOp",EDGE,"E3.filletArc"),sQuery(id+"F0.wireOp",EDGE,"E4.filletArc"),sQuery(id+"F0.wireOp",EDGE,"E39"),sQuery(id+"F0.wireOp",EDGE,"E40"),sQuery(id+"F0.wireOp",EDGE,"E41"),sQuery(id+"F0.wireOp",EDGE,"E42"),sQuery(id+"F0.wireOp",EDGE,"E43"),sQuery(id+"F0.wireOp",EDGE,"E44"),sQuery(id+"F0.wireOp",EDGE,"E45"),sQuery(id+"F0.wireOp",EDGE,"E46"),sQuery(id+"F0.wireOp",EDGE,"E47"),sQuery(id+"F0.wireOp",EDGE,"E48"),sQuery(id+"F0.wireOp",EDGE,"E49"),sQuery(id+"F0.wireOp",EDGE,"E50"),sQuery(id+"F0.wireOp",EDGE,"E51"),sQuery(id+"F0.wireOp",EDGE,"E52"),sQuery(id+"F0.wireOp",EDGE,"E54.MirrorCS"),sQuery(id+"F0.wireOp",EDGE,"E55.MirrorCS"),sQuery(id+"F0.wireOp",EDGE,"E56.MirrorCS"),sQuery(id+"F0.wireOp",EDGE,"E57.MirrorCS"),sQuery(id+"F0.wireOp",EDGE,"E58.MirrorCS"),sQuery(id+"F0.wireOp",EDGE,"E59.MirrorCS"),sQuery(id+"F0.wireOp",EDGE,"E60.MirrorCS"),sQuery(id+"F0.wireOp",EDGE,"E61.MirrorCS"),sQuery(id+"F0.wireOp",EDGE,"E62.MirrorCS"),sQuery(id+"F0.wireOp",EDGE,"E63.MirrorCS"),sQuery(id+"F0.wireOp",EDGE,"E64.MirrorCS"),sQuery(id+"F0.wireOp",EDGE,"E65.MirrorCS"),sQuery(id+"F0.wireOp",EDGE,"E66.MirrorCS"),sQuery(id+"F0.wireOp",EDGE,"E67.MirrorCS"),sQuery(id+"F0.wireOp",EDGE,"E68.MirrorCS"),sQuery(id+"F0.wireOp",EDGE,"E82")])]});
            booleanBodies(context, id + "F6", {"operationType" : BooleanOperationType.SUBTRACTION, "tools" : qUnion([Q0, Q1, Q2, Q3, Q4, Q5]), "targets" : qUnion([Q6])});
        }
        {
            var Q0;
            Q0=makeQuery(id+"F6.opBoolean","SPLIT",FACE,{"disambiguationData":[TD([makeQuery(id+"F3.opExtrude","SWEPT_FACE",FACE,{"disambiguationData":[OSD([sQuery(id+"F2.wireOp",EDGE,"E83.8")])]})])],"derivedFrom":makeQuery(id+"F1.opExtrude","CAP_FACE",FACE,{"disambiguationData":[OSD([sQuery(id+"F0.wireOp",EDGE,"E0.bottom"),sQuery(id+"F0.wireOp",EDGE,"E0.top"),sQuery(id+"F0.wireOp",EDGE,"E0.left"),sQuery(id+"F0.wireOp",EDGE,"E0.right"),sQuery(id+"F0.wireOp",EDGE,"E1.filletArc"),sQuery(id+"F0.wireOp",EDGE,"E2.filletArc"),sQuery(id+"F0.wireOp",EDGE,"E3.filletArc"),sQuery(id+"F0.wireOp",EDGE,"E4.filletArc"),sQuery(id+"F0.wireOp",EDGE,"E39"),sQuery(id+"F0.wireOp",EDGE,"E40"),sQuery(id+"F0.wireOp",EDGE,"E41"),sQuery(id+"F0.wireOp",EDGE,"E42"),sQuery(id+"F0.wireOp",EDGE,"E43"),sQuery(id+"F0.wireOp",EDGE,"E44"),sQuery(id+"F0.wireOp",EDGE,"E45"),sQuery(id+"F0.wireOp",EDGE,"E46"),sQuery(id+"F0.wireOp",EDGE,"E47"),sQuery(id+"F0.wireOp",EDGE,"E48"),sQuery(id+"F0.wireOp",EDGE,"E49"),sQuery(id+"F0.wireOp",EDGE,"E50"),sQuery(id+"F0.wireOp",EDGE,"E51"),sQuery(id+"F0.wireOp",EDGE,"E52"),sQuery(id+"F0.wireOp",EDGE,"E54.MirrorCS"),sQuery(id+"F0.wireOp",EDGE,"E55.MirrorCS"),sQuery(id+"F0.wireOp",EDGE,"E56.MirrorCS"),sQuery(id+"F0.wireOp",EDGE,"E57.MirrorCS"),sQuery(id+"F0.wireOp",EDGE,"E58.MirrorCS"),sQuery(id+"F0.wireOp",EDGE,"E59.MirrorCS"),sQuery(id+"F0.wireOp",EDGE,"E60.MirrorCS"),sQuery(id+"F0.wireOp",EDGE,"E61.MirrorCS"),sQuery(id+"F0.wireOp",EDGE,"E62.MirrorCS"),sQuery(id+"F0.wireOp",EDGE,"E63.MirrorCS"),sQuery(id+"F0.wireOp",EDGE,"E64.MirrorCS"),sQuery(id+"F0.wireOp",EDGE,"E65.MirrorCS"),sQuery(id+"F0.wireOp",EDGE,"E66.MirrorCS"),sQuery(id+"F0.wireOp",EDGE,"E67.MirrorCS"),sQuery(id+"F0.wireOp",EDGE,"E68.MirrorCS"),sQuery(id+"F0.wireOp",EDGE,"E82")])],"isStart":false})});
            var sketch = newSketch(context, id + "F7", { "sketchPlane" : qUnion([Q0])});
            skLineSegment(sketch, "E99", {"start": v(10.02, 2.1) * mm, "end": v(10.02, -11.38) * mm});
            skLineSegment(sketch, "E100", {"start": v(10.02, -11.38) * mm, "end": v(11.02, -11.38) * mm});
            skLineSegment(sketch, "E101", {"start": v(11.02, -11.38) * mm, "end": v(11.02, 2.14) * mm});
            skLineSegment(sketch, "E102", {"start": v(11.02, 2.14) * mm, "end": v(10.02, 2.1) * mm});
            skSolve(sketch);
        }
        {
            var Q0;
            {var subQ0=sQuery(id+"F7.wireOp",EDGE,"E102");Q0=makeQuery(id+"F7.imprint","IMPRINT",FACE,{"disambiguationData":[TD([[makeQuery(id+"F7.imprint","IMPRINT",EDGE,{"derivedFrom":subQ0}),1.0]])]});}
            var Q1;
            {var subQ0=sQuery(id+"F7.wireOp",EDGE,"E100");Q1=makeQuery(id+"F7.imprint","IMPRINT",FACE,{"disambiguationData":[TD([[makeQuery(id+"F7.imprint","IMPRINT",EDGE,{"derivedFrom":subQ0}),1.0]])]});}
            var Q2;
            {var subQ0=sQuery(id+"F0.wireOp",EDGE,"E66.MirrorCS");var subQ1=sQuery(id+"F0.wireOp",EDGE,"E63.MirrorCS");var subQ2=sQuery(id+"F0.wireOp",EDGE,"E60.MirrorCS");var subQ3=sQuery(id+"F0.wireOp",EDGE,"E82");var subQ4=sQuery(id+"F0.wireOp",EDGE,"E57.MirrorCS");var subQ5=sQuery(id+"F0.wireOp",EDGE,"E68.MirrorCS");var subQ6=sQuery(id+"F0.wireOp",EDGE,"E56.MirrorCS");var subQ7=sQuery(id+"F0.wireOp",EDGE,"E67.MirrorCS");var subQ8=sQuery(id+"F0.wireOp",EDGE,"E55.MirrorCS");var subQ9=sQuery(id+"F0.wireOp",EDGE,"E54.MirrorCS");var subQ10=sQuery(id+"F0.wireOp",EDGE,"E64.MirrorCS");var subQ11=sQuery(id+"F0.wireOp",EDGE,"E62.MirrorCS");var subQ12=sQuery(id+"F0.wireOp",EDGE,"E50");var subQ13=sQuery(id+"F0.wireOp",EDGE,"E61.MirrorCS");var subQ14=sQuery(id+"F0.wireOp",EDGE,"E59.MirrorCS");var subQ15=sQuery(id+"F0.wireOp",EDGE,"E47");var subQ16=sQuery(id+"F0.wireOp",EDGE,"E58.MirrorCS");var subQ17=sQuery(id+"F0.wireOp",EDGE,"E40");var subQ18=sQuery(id+"F0.wireOp",EDGE,"E39");var subQ19=sQuery(id+"F0.wireOp",EDGE,"E4.filletArc");var subQ20=sQuery(id+"F0.wireOp",EDGE,"E3.filletArc");var subQ21=sQuery(id+"F0.wireOp",EDGE,"E2.filletArc");var subQ22=sQuery(id+"F0.wireOp",EDGE,"E1.filletArc");var subQ23=sQuery(id+"F0.wireOp",EDGE,"E65.MirrorCS");var subQ24=sQuery(id+"F0.wireOp",EDGE,"E0.bottom");var subQ25=sQuery(id+"F0.wireOp",EDGE,"E0.top");var subQ26=sQuery(id+"F0.wireOp",EDGE,"E0.left");var subQ27=sQuery(id+"F0.wireOp",EDGE,"E0.right");var subQ28=sQuery(id+"F0.wireOp",EDGE,"E41");var subQ29=sQuery(id+"F0.wireOp",EDGE,"E42");var subQ30=sQuery(id+"F0.wireOp",EDGE,"E43");var subQ31=sQuery(id+"F0.wireOp",EDGE,"E44");var subQ32=sQuery(id+"F0.wireOp",EDGE,"E45");var subQ33=sQuery(id+"F0.wireOp",EDGE,"E46");var subQ34=sQuery(id+"F0.wireOp",EDGE,"E48");var subQ35=sQuery(id+"F0.wireOp",EDGE,"E49");var subQ36=sQuery(id+"F0.wireOp",EDGE,"E51");var subQ37=sQuery(id+"F0.wireOp",EDGE,"E52");Q2=makeQuery(id+"F6.opBoolean","SPLIT",FACE,{"disambiguationData":[TD([makeQuery(id+"F1.opExtrude","SWEPT_FACE",FACE,{"disambiguationData":[OSD([subQ25])]})])],"derivedFrom":makeQuery(id+"F1.opExtrude","CAP_FACE",FACE,{"disambiguationData":[OSD([subQ24,subQ25,subQ26,subQ27,subQ22,subQ21,subQ20,subQ19,subQ18,subQ17,subQ28,subQ29,subQ30,subQ31,subQ32,subQ33,subQ15,subQ34,subQ35,subQ12,subQ36,subQ37,subQ9,subQ8,subQ6,subQ4,subQ16,subQ14,subQ2,subQ13,subQ11,subQ1,subQ10,subQ23,subQ0,subQ7,subQ5,subQ3])],"isStart":true})});}
            extrude(context, id + "F8", {"entities" : qUnion([Q0, Q1]), "operationType" : NewBodyOperationType.ADD, "endBound" : BoundingType.UP_TO_SURFACE, "oppositeDirection" : true, "depth" : 25 * mm, "endBoundEntityFace" : qUnion([Q2]), "offsetDistance" : 25 * mm});
        }
    });
